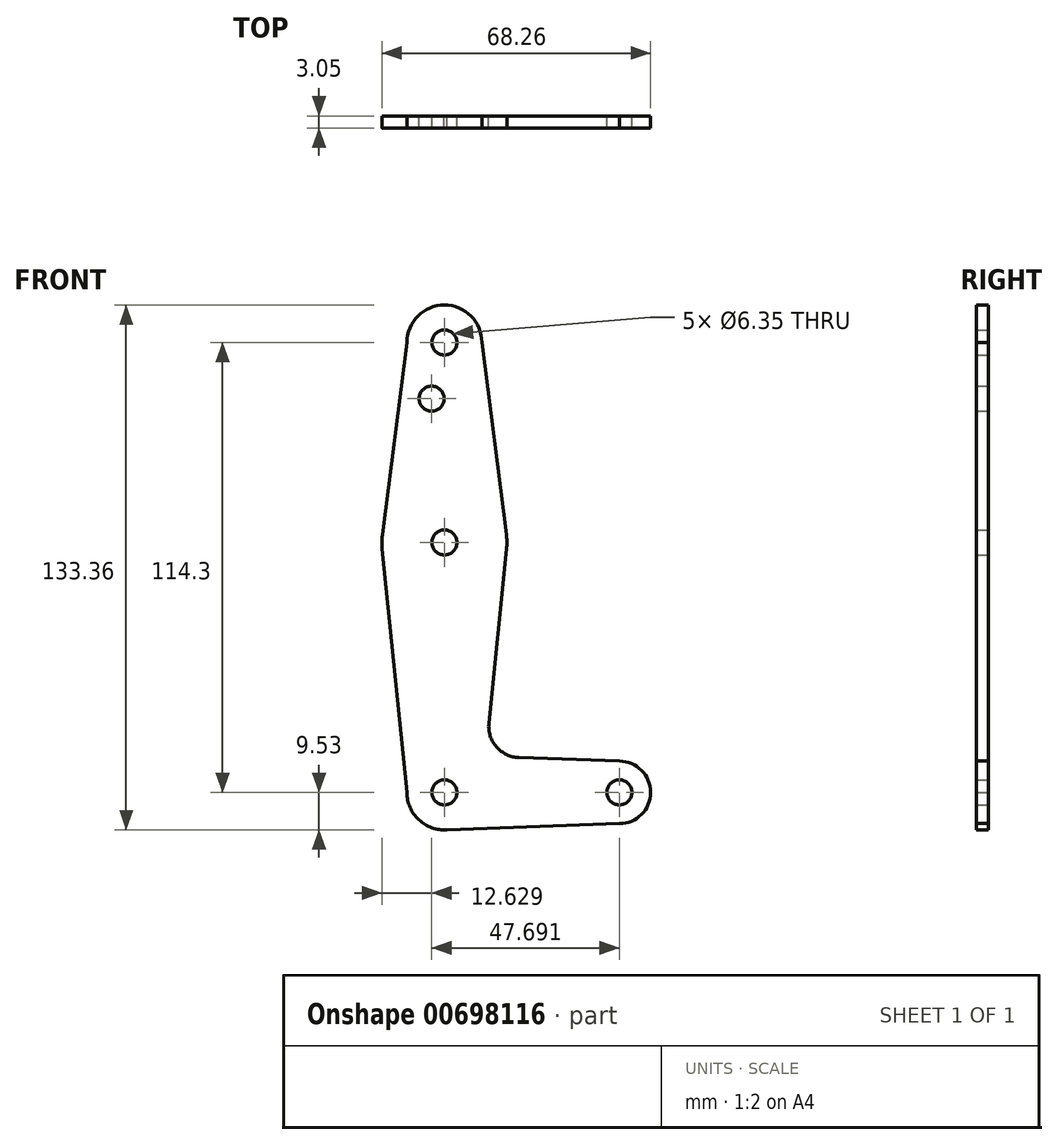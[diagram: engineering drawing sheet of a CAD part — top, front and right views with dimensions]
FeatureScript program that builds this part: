
annotation { "Feature Type Name" : "Feature", "Feature Type Description" : "" }
export const myFeature = defineFeature(function(context is Context, id is Id, definition is map)
    precondition{}
    {
        {
            var Q0;
            Q0=qCreatedBy(makeId("Front.planeOp"),FACE);
            var sketch = newSketch(context, id + "F0", { "sketchPlane" : qUnion([Q0])});
            skLineSegment(sketch, "E0", {"start": v(0, 0) * mm, "end": v(0, 114.3) * mm, "construction": true});
            skLineSegment(sketch, "E1", {"start": v(0, 0) * mm, "end": v(44.45, 0) * mm, "construction": true});
            skCircle(sketch, "E2", {"center": v(0, 0) * mm, "radius": 9.53 * mm});
            skCircle(sketch, "E3", {"center": v(44.45, 0) * mm, "radius": 7.94 * mm});
            skCircle(sketch, "E4", {"center": v(0, 114.3) * mm, "radius": 9.53 * mm});
            skCircle(sketch, "E5", {"center": v(0, 63.5) * mm, "radius": 15.88 * mm});
            skLineSegment(sketch, "E6", {"start": v(0, -9.53) * mm, "end": v(44.45, -7.94) * mm});
            skLineSegment(sketch, "E7", {"start": v(18.93, 8.85) * mm, "end": v(44.45, 7.94) * mm});
            skLineSegment(sketch, "E8", {"start": v(-9.53, 0) * mm, "end": v(-15.8, 61.9) * mm});
            skLineSegment(sketch, "E9", {"start": v(11.3, 17.6) * mm, "end": v(15.8, 61.9) * mm});
            skLineSegment(sketch, "E10", {"start": v(-9.53, 114.3) * mm, "end": v(-15.75, 65.5) * mm});
            skLineSegment(sketch, "E11", {"start": v(9.52, 114.3) * mm, "end": v(15.75, 65.5) * mm});
            skCircle(sketch, "E12", {"center": v(0, 114.3) * mm, "radius": 3.18 * mm});
            skCircle(sketch, "E13", {"center": v(-3.24, 100.03) * mm, "radius": 3.18 * mm});
            skCircle(sketch, "E14", {"center": v(0, 0) * mm, "radius": 3.18 * mm});
            skCircle(sketch, "E15", {"center": v(44.45, 0) * mm, "radius": 3.18 * mm});
            skCircle(sketch, "E16", {"center": v(0, 63.5) * mm, "radius": 3.18 * mm});
            skPoint(sketch, "E17.newPointB", {"position": v(0, 9.53) * mm});
            skArc(sketch, "E17.filletArc", {"start": v(11.3, 17.6) * mm, "mid": v(13.22, 11.57) * mm, "end": v(18.93, 8.85) * mm});
            skSolve(sketch);
        }
        {
            var Q0;
            Q0 = qSketchRegion(id + "F0", true);
            extrude(context, id + "F1", {"entities" : qUnion([Q0]), "depth" : 3.05 * mm, "offsetDistance" : 25.4 * mm});
        }
    });
